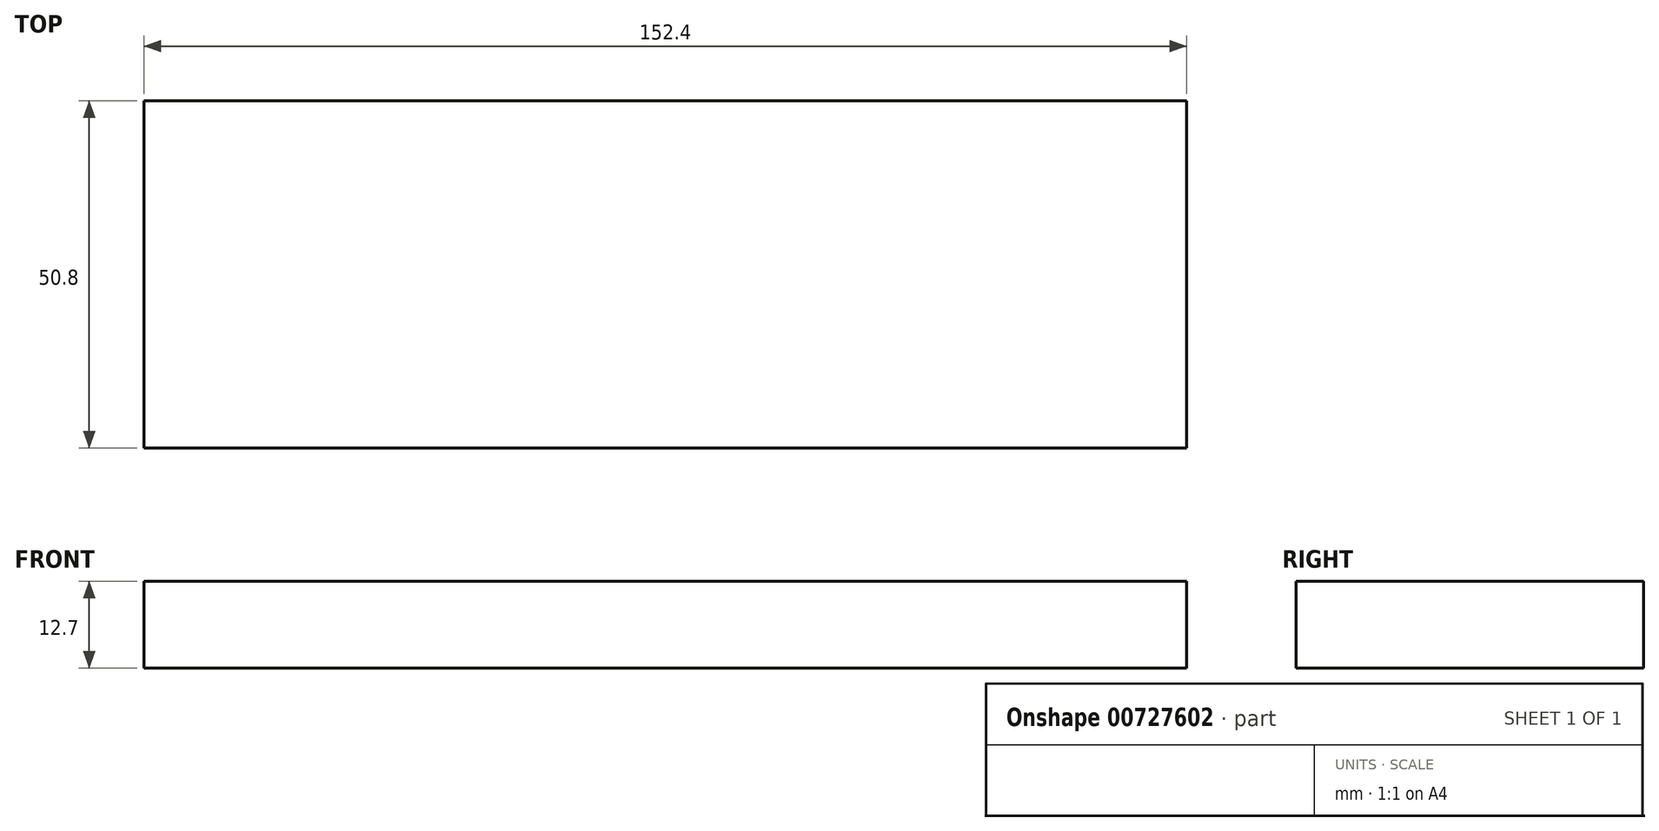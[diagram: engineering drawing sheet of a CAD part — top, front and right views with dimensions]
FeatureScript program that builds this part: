
annotation { "Feature Type Name" : "Feature", "Feature Type Description" : "" }
export const myFeature = defineFeature(function(context is Context, id is Id, definition is map)
    precondition{}
    {
        {
            var Q0;
            Q0=qCreatedBy(makeId("Top.planeOp"),FACE);
            var sketch = newSketch(context, id + "F0", { "sketchPlane" : qUnion([Q0])});
            skLineSegment(sketch, "E0.bottom", {"start": v(-76.2, 25.4) * mm, "end": v(76.2, 25.4) * mm});
            skLineSegment(sketch, "E0.top", {"start": v(-76.2, -25.4) * mm, "end": v(76.2, -25.4) * mm});
            skLineSegment(sketch, "E0.left", {"start": v(-76.2, 25.4) * mm, "end": v(-76.2, -25.4) * mm});
            skLineSegment(sketch, "E0.right", {"start": v(76.2, 25.4) * mm, "end": v(76.2, -25.4) * mm});
            skPoint(sketch, "E0.middle", {"position": v(0, 0) * mm});
            skSolve(sketch);
        }
        {
            var Q0;
            Q0 = qSketchRegion(id + "F0", true);
            extrude(context, id + "F1", {"entities" : qUnion([Q0]), "depth" : 12.7 * mm, "offsetDistance" : 25.4 * mm});
        }
    });
